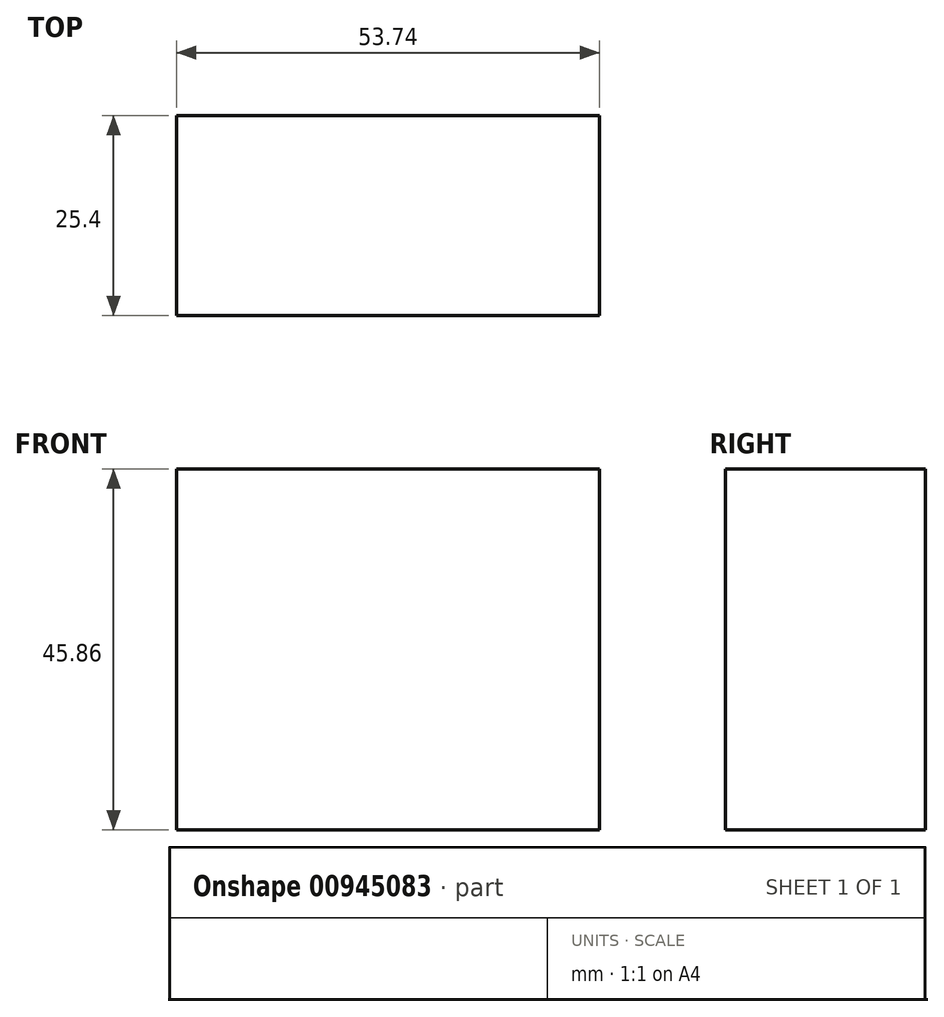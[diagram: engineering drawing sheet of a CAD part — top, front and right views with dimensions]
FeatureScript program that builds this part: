
annotation { "Feature Type Name" : "Feature", "Feature Type Description" : "" }
export const myFeature = defineFeature(function(context is Context, id is Id, definition is map)
    precondition{}
    {
        {
            var Q0;
            Q0=qCreatedBy(makeId("Front.planeOp"),FACE);
            var sketch = newSketch(context, id + "F0", { "sketchPlane" : qUnion([Q0])});
            skLineSegment(sketch, "E0.bottom", {"start": v(-26.87, -22.93) * mm, "end": v(26.87, -22.93) * mm});
            skLineSegment(sketch, "E0.top", {"start": v(-26.87, 22.93) * mm, "end": v(26.87, 22.93) * mm});
            skLineSegment(sketch, "E0.left", {"start": v(-26.87, -22.93) * mm, "end": v(-26.87, 22.93) * mm});
            skLineSegment(sketch, "E0.right", {"start": v(26.87, -22.93) * mm, "end": v(26.87, 22.93) * mm});
            skPoint(sketch, "E0.middle", {"position": v(0, 0) * mm});
            skSolve(sketch);
        }
        {
            var Q0;
            Q0 = qSketchRegion(id + "F0", true);
            extrude(context, id + "F1", {"entities" : qUnion([Q0]), "endBound" : BoundingType.SYMMETRIC, "depth" : 25.4 * mm, "offsetDistance" : 25.4 * mm});
        }
    });
